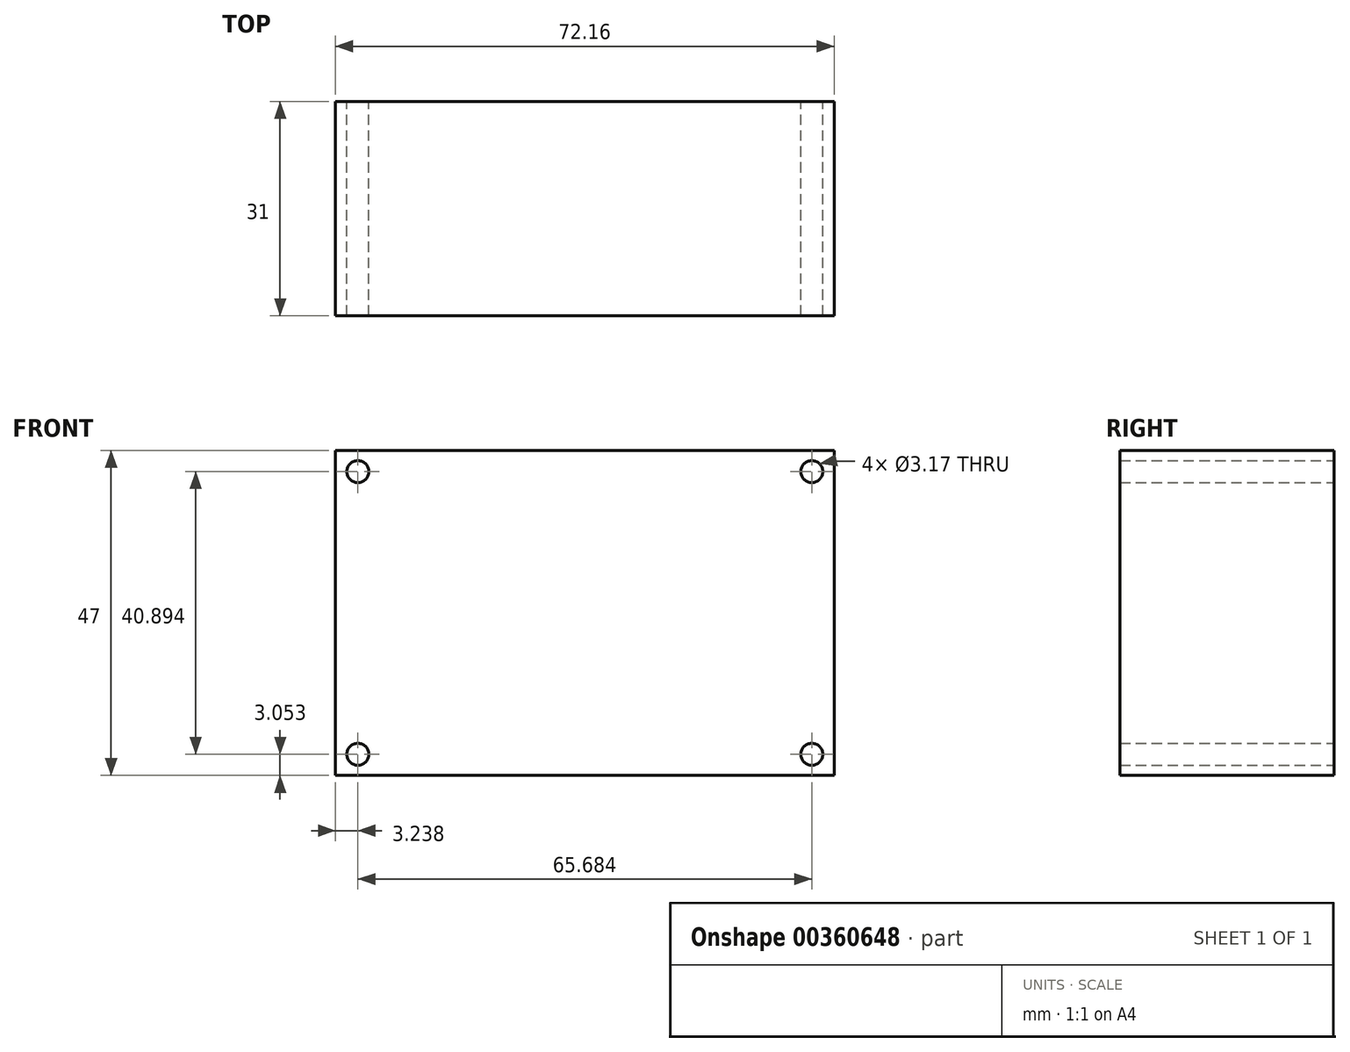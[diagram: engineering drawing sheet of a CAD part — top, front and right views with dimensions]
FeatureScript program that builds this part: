
annotation { "Feature Type Name" : "Feature", "Feature Type Description" : "" }
export const myFeature = defineFeature(function(context is Context, id is Id, definition is map)
    precondition{}
    {
        {
            var Q0;
            Q0=qCreatedBy(makeId("Front.planeOp"),FACE);
            var sketch = newSketch(context, id + "F0", { "sketchPlane" : qUnion([Q0])});
            skLineSegment(sketch, "E0.bottom", {"start": v(-36.08, 23.5) * mm, "end": v(36.08, 23.5) * mm});
            skLineSegment(sketch, "E0.top", {"start": v(-36.08, -23.5) * mm, "end": v(36.08, -23.5) * mm});
            skLineSegment(sketch, "E0.left", {"start": v(-36.08, 23.5) * mm, "end": v(-36.08, -23.5) * mm});
            skLineSegment(sketch, "E0.right", {"start": v(36.08, 23.5) * mm, "end": v(36.08, -23.5) * mm});
            skPoint(sketch, "E1", {"position": v(0, 23.5) * mm});
            skPoint(sketch, "E2", {"position": v(-36.08, 0) * mm});
            skLineSegment(sketch, "E3.bottom", {"start": v(-32.84, 20.45) * mm, "end": v(32.84, 20.45) * mm, "construction": true});
            skLineSegment(sketch, "E3.top", {"start": v(-32.84, -20.45) * mm, "end": v(32.84, -20.45) * mm, "construction": true});
            skLineSegment(sketch, "E3.left", {"start": v(-32.84, 20.45) * mm, "end": v(-32.84, -20.45) * mm, "construction": true});
            skLineSegment(sketch, "E3.right", {"start": v(32.84, 20.45) * mm, "end": v(32.84, -20.45) * mm, "construction": true});
            skPoint(sketch, "E4", {"position": v(0, 20.45) * mm});
            skPoint(sketch, "E5", {"position": v(-32.84, 0) * mm});
            skCircle(sketch, "E6", {"center": v(-32.84, 20.45) * mm, "radius": 1.59 * mm});
            skCircle(sketch, "E7", {"center": v(-32.84, -20.45) * mm, "radius": 1.59 * mm});
            skCircle(sketch, "E8", {"center": v(32.84, -20.45) * mm, "radius": 1.59 * mm});
            skCircle(sketch, "E9", {"center": v(32.84, 20.45) * mm, "radius": 1.59 * mm});
            skSolve(sketch);
        }
        {
            var Q0;
            Q0 = qSketchRegion(id + "F0", true);
            extrude(context, id + "F1", {"entities" : qUnion([Q0]), "depth" : 31 * mm});
        }
    });
